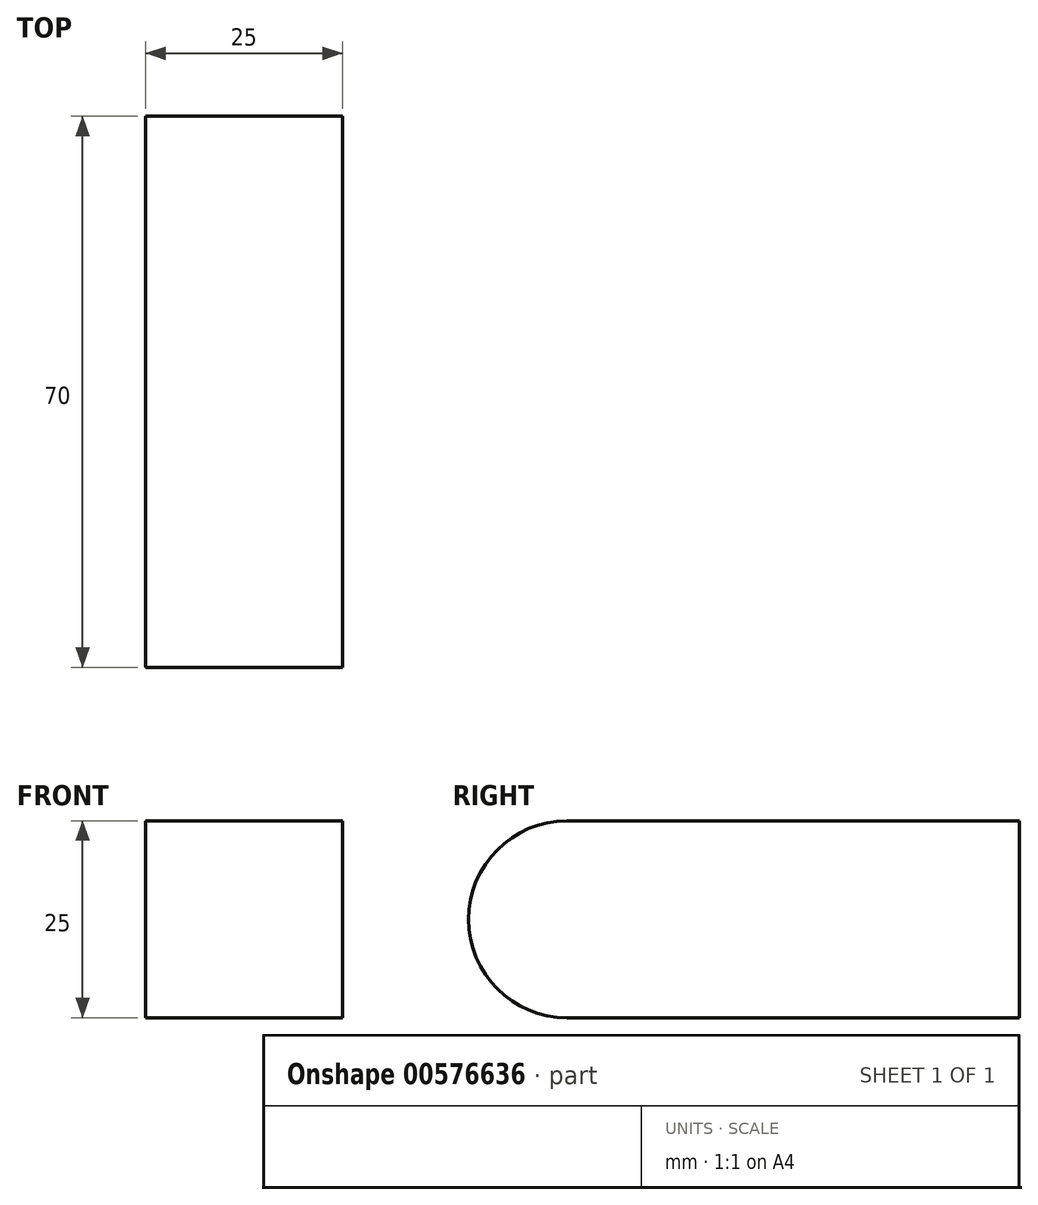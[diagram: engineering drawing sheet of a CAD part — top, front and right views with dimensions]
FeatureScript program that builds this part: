
annotation { "Feature Type Name" : "Feature", "Feature Type Description" : "" }
export const myFeature = defineFeature(function(context is Context, id is Id, definition is map)
    precondition{}
    {
        {
            var Q0;
            Q0=qCreatedBy(makeId("Right.planeOp"),FACE);
            var sketch = newSketch(context, id + "F0", { "sketchPlane" : qUnion([Q0])});
            skLineSegment(sketch, "E0.bottom", {"start": v(32.27, -12.5) * mm, "end": v(-25.23, -12.5) * mm});
            skLineSegment(sketch, "E0.top", {"start": v(32.27, 12.5) * mm, "end": v(-25.23, 12.5) * mm});
            skLineSegment(sketch, "E0.left", {"start": v(32.27, -12.5) * mm, "end": v(32.27, 12.5) * mm});
            skPoint(sketch, "E0.middle", {"position": v(3.52, 0) * mm});
            skArc(sketch, "E1", {"start": v(-25.23, 12.5) * mm, "mid": v(-37.73, 0) * mm, "end": v(-25.23, -12.5) * mm});
            skSolve(sketch);
        }
        {
            var Q0;
            Q0=makeQuery(id+"F0.imprint","IMPRINT",FACE,{"disambiguationData":[TD([[makeQuery(id+"F0.imprint","IMPRINT",EDGE,{"derivedFrom":sQuery(id+"F0.wireOp",EDGE,"E0.bottom")}),-1.0]])]});
            extrude(context, id + "F1", {"entities" : qUnion([Q0]), "depth" : 25 * mm, "offsetDistance" : 25 * mm});
        }
    });
